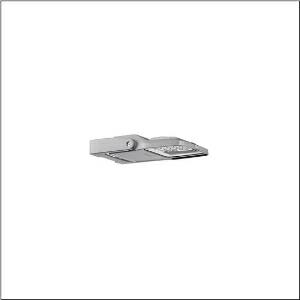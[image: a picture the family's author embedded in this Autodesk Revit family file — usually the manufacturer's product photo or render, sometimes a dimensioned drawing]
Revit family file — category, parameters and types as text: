
# Revit family: floodlight_fl_21_iq_micro___pl43_5xa7761a2a2a_4945
name_source: partatom
category: Lighting Fixtures
units: mm (PartAtom-declared; Revit-internal decimal feet)

## family parameters
Cut with Voids When Loaded = No
Host = Face
Light Source = No
Part Type = Normal
Room Calculation Point = No
Round Connector Dimension = Use Diameter
Shared = No

## types (1)
- --- (1 x LED, 3040 lm, 23.1 W, 3000K)
    Apparent Load = 23 VA
    CIE Flux Codes = 29 80 99 100 100
    Color Rendering = 70
    Color Temperature = 3000K
    Default Elevation = 1800 mm
    Description = Floodlight FL 21 iQ micro, floodlight, primary light control with lens, of PMMA, primary optical cover: protective disc, of toughened safety glass, transparent, light distribution: PL43, light emission: direct distribution, installation type: surface-mounted, LED, High Power LED, rated luminous flux: 3.040lm, luminous efficacy: 132lm/W, light colour: 730, colour temperature: 3000K, control gear: iQ Comfort/DALI, control: optimised constant luminous flux control (CLO 2.0), Desk-Remote (wireless, voltage-free reading and setting of iQ features in the workshop via application-optimized NFC function/RFID function), Light-Fading, Smart-Wire, Night-Set, Lumen-Switch, Temp-Guard, Auto-Match, with terminal, 6-pole, mains connection: 220..240V, AC, 50/60Hz, start of lifetime: 23W, end of service life: 24W, reduction: 11W, luminaire housing, of diecast aluminium, powder-coated, Siteco® metallic grey (DB 702S), corrosivity category C5 mid according to DIN EN ISO 12944, suitable for swimming pools, chlorine-resistant, sealing non-destructively replaceable, design bracket, of diecast aluminium, powder-coated, Siteco® metallic grey (DB 702S), protection rating (complete): IP66, insulation class (complete): insulation class II (safety insulation), certification: CE, ENEC, VDE, protection symbol: D, impact resistance: IK07, permissible operating ambient temperature: -40..+40°C, permissible operating ambient temperature for outdoor applications: -40..+50°C, standard: DIN EN 12944, LABS conformity tested according to VDMA 24364:2018-05, packaging unit: 1 piece

Light Distribution: PL43
    Height = 65 mm
    Lamp = 1 x LED
    Lamp Light Flux = 3040 lm
    Lamp Power = 23.1 W
    Lamp count = 1
    Length = 312 mm
    Luminous efficacy = 132 lm/W
    Manufacturer = Siteco
    ModVariant = No
    Model = 5XA7761A2A2A
    Mounting Place = Wall
    Mounting Type = Surface mounted
    Number of Poles = 1
    OnlyDefault = Yes
    Power Factor = 1
    Product Name = Floodlight FL 21 iQ micro | PL43
    Product group = floodlight | wall mounted
    ProductGroupID = 2001
    Protection Class = Protection class II
    Protection Degree = IP 66
    RLX_Detail_Level = 1
    RLX_Emergency_Light_Flux = 0 lm
    RLX_Emergency_Type = 0
    RLX_Emergency_Type_DB = No
    RlxData = <blob elided: 97453 chars, md5=7c2635f2>
    Socket = socket
    Standby Power = 0 W
    System Light Flux = 3040 lm
    System Power = 23 W
    Type Comments = factory setting: luminous flux: 100 % | dim-lin: 254 | 455 mA
    Type Image = l_1006878.jpg
    URL = http://relux.com
    VarID = @adj_176864
    Voltage = 0 V
    Weight = 0.00 kg
    Width = 230 mm

## geometry (parser evidence)
native form markers: Blend x4, Sweep x12
no freeform markers — native parametric forms only
